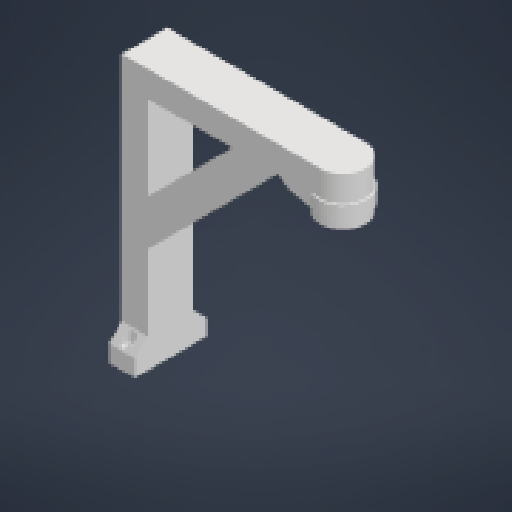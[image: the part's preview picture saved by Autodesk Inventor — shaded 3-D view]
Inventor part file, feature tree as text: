
AUTODESK INVENTOR PART (.ipt)
format: ipt  version: 2023.2 (Build 272271000, 271)  size: 288,256 bytes
history: native  units: in
note: dims shown in document units (in); Inventor stores cm internally (conversion verified against a paired STEP export)
features: sketch x13, extrude x10, thicken_offset x2, fillet x2, loft x1, chamfer x1, direct_edit x1, move_body x1
ambient origin geometry x8: Origin, YZ Plane, XZ Plane, XY Plane, X Axis, Y Axis, Z Axis, Center Point
bodies: Solid1 (feature_tree)
feature tree (31):
  extrude  "Extrusion1"  Depth=0.7874in
  extrude  "Extrusion2"  Depth=0.1575in
  extrude  "Extrusion3"  Depth=0.1181in TaperAngle=0.0deg
  extrude  "Extrusion4"  Depth=0.7874in
  extrude  "Extrusion5"  Depth=6.6929in
  thicken_offset  "Thicken1"
  thicken_offset  "Thicken2"
  loft  "Loft3"
  extrude  "Extrusion6"  Depth=0.3937in
  chamfer  "Chamfer1"  Distance=1.378in
  extrude  "Extrusion7"  TaperAngle=0.0deg  [1 undecoded]
  extrude  "Extrusion8"  TaperAngle=0.0deg  [1 undecoded]
  extrude  "Extrusion10"  Depth=0.3937in TaperAngle=0.0deg
  fillet  "Fillet1"  Radius=0.3937in
  fillet  "Fillet2"  Radius=0.315in
  extrude  "Extrusion11"  Depth=0.1969in
  sketch  "Sketch16"  dims[d36=1.378in d37=1.378in d38=0.0in d39=90.0deg d40=0.0in d41=90.0deg d42=0.3937in d43=0.0in d44=0.3937in d45=0.0787in d46=45.0deg d47=0.315in d48=0.315in d49=0.3937in d50=0.0in d51=1.4961in d52=0.3937in d53=0.0in d56=0.3543in d57=0.0in d58=1.5748in d59=0.689in d60=0.6299in d61=0.6299in d62=0.1181in d63=0.1969in d64=1.5748in d66=360.0deg d68=0.1969in d69=0.0in d70=0.0in d71=0.0in d72=-0.1969in d18=0.0197in d19=0.0344in d20=0.0197in d21=0.0344in]
  direct_edit  "Direct Edit1"
  sketch  "Sketch1"  dims[d0=0.7874in d1=2.1654in]
  sketch  "Sketch2"  dims[d2=0.1181in d3=0.0in d4=0.1575in]
  sketch  "Sketch3"  dims[d5=0.1575in d6=0.1181in d7=0.0in]
  sketch  "Sketch4"  dims[d8=0.7874in d9=1.378in]
  sketch  "Sketch5"  dims[d10=7.0079in d11=0.0in d12=6.6929in]
  sketch  "Sketch8"  dims[d13=1.378in d14=0.3937in d15=0.0in]
  sketch  "Sketch9"  dims[d16=0.6772in d17=0.0in d26=0.3937in]
  sketch  "Sketch10"  dims[d27=0.3937in]
  sketch  "Sketch11"  dims[d28=0.3937in]
  sketch  "Sketch12"  dims[d29=0.3937in]
  sketch  "Sketch14"  dims[d34=1.378in]
  sketch  "Sketch15"  dims[d35=1.378in]
  move_body  "Move1"
note: 2 required parameter values undecoded (feature->parameter linkage not recoverable at this tier; creation-order binding heuristic only, values carry confidence <= 0.55)
